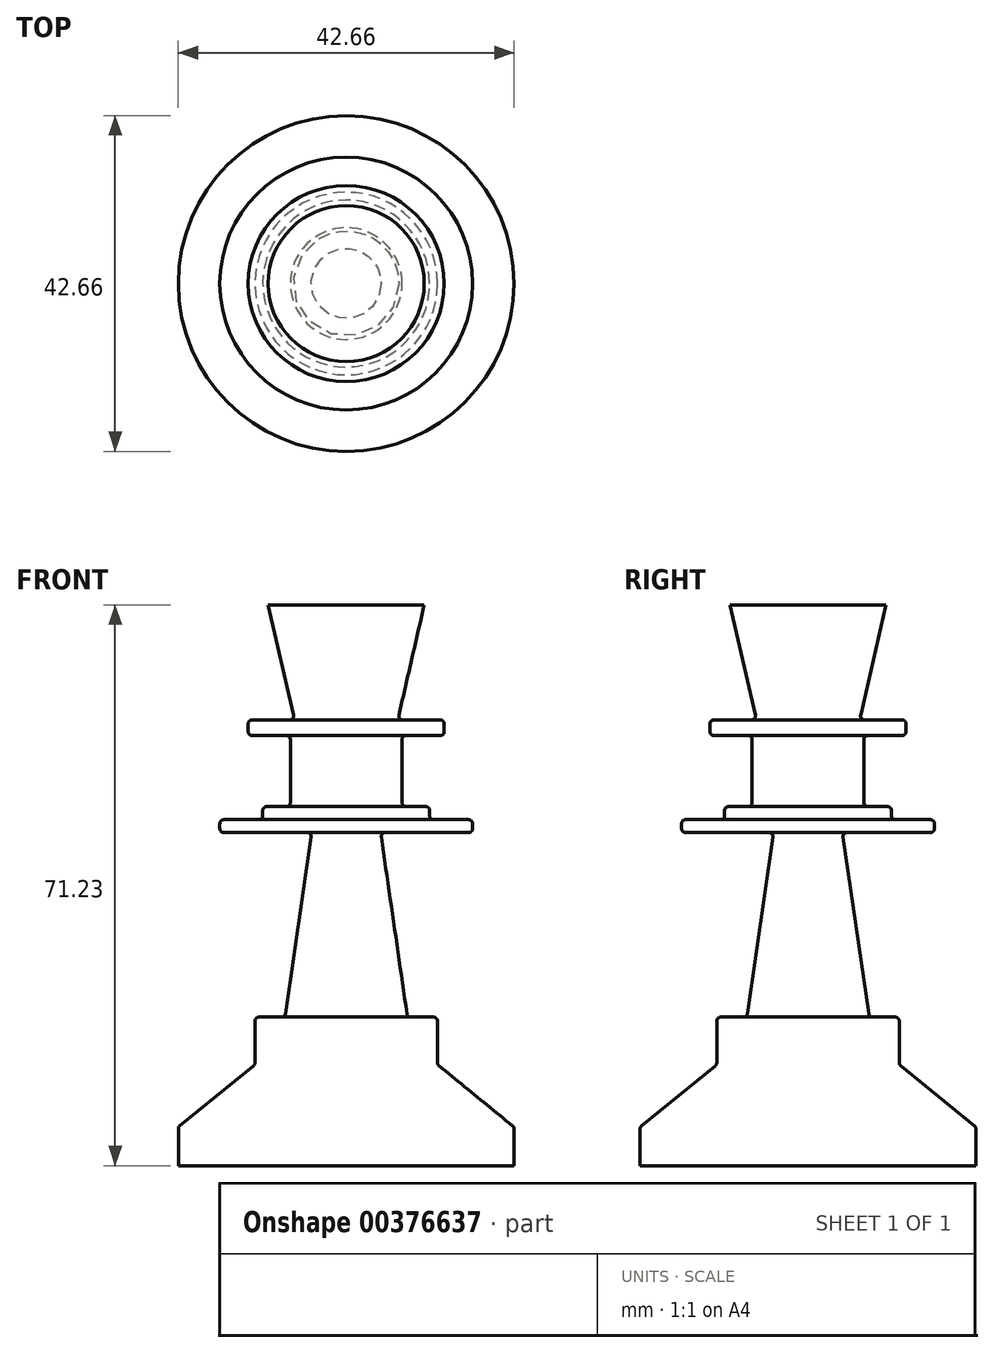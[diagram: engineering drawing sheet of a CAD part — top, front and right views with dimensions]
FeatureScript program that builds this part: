
annotation { "Feature Type Name" : "Feature", "Feature Type Description" : "" }
export const myFeature = defineFeature(function(context is Context, id is Id, definition is map)
    precondition{}
    {
        {
            var Q0;
            Q0=qCreatedBy(makeId("Front.planeOp"),FACE);
            var sketch = newSketch(context, id + "F0", { "sketchPlane" : qUnion([Q0])});
            skLineSegment(sketch, "E0", {"start": v(0, 71.23) * mm, "end": v(-9.91, 71.23) * mm});
            skLineSegment(sketch, "E1", {"start": v(-9.91, 71.23) * mm, "end": v(-6.7, 57.26) * mm});
            skLineSegment(sketch, "E2", {"start": v(-7.19, 56.63) * mm, "end": v(-11.95, 56.63) * mm});
            skLineSegment(sketch, "E3", {"start": v(-12.45, 56.13) * mm, "end": v(-12.45, 55.15) * mm});
            skLineSegment(sketch, "E4", {"start": v(-11.95, 54.64) * mm, "end": v(-7.6, 54.64) * mm});
            skLineSegment(sketch, "E5", {"start": v(-7.1, 54.13) * mm, "end": v(-7.1, 46.13) * mm});
            skLineSegment(sketch, "E6", {"start": v(-7.6, 45.63) * mm, "end": v(-10.1, 45.63) * mm});
            skLineSegment(sketch, "E7", {"start": v(-10.6, 45.12) * mm, "end": v(-10.6, 44.46) * mm});
            skLineSegment(sketch, "E8", {"start": v(-11.1, 43.95) * mm, "end": v(-15.55, 43.95) * mm});
            skLineSegment(sketch, "E9", {"start": v(-16.06, 43.45) * mm, "end": v(-16.06, 42.82) * mm});
            skLineSegment(sketch, "E10", {"start": v(-15.55, 42.31) * mm, "end": v(-4.96, 42.31) * mm});
            skLineSegment(sketch, "E11", {"start": v(-4.45, 41.73) * mm, "end": v(-7.71, 19.3) * mm});
            skLineSegment(sketch, "E12", {"start": v(-21.33, 4.66) * mm, "end": v(-21.33, 0) * mm});
            skLineSegment(sketch, "E13", {"start": v(-21.33, 0) * mm, "end": v(0, 0) * mm});
            skLineSegment(sketch, "E14", {"start": v(-8.22, 18.87) * mm, "end": v(-11.09, 18.87) * mm});
            skLineSegment(sketch, "E15", {"start": v(-11.6, 18.37) * mm, "end": v(-11.6, 13.08) * mm});
            skLineSegment(sketch, "E16", {"start": v(-21.14, 5.05) * mm, "end": v(-11.78, 12.69) * mm});
            skLineSegment(sketch, "E17", {"start": v(0, 71.23) * mm, "end": v(0, 0) * mm});
            skPoint(sketch, "E18.visualSharp", {"position": v(-6.55, 56.63) * mm});
            skArc(sketch, "E18.filletArc", {"start": v(-7.19, 56.63) * mm, "mid": v(-6.79, 56.82) * mm, "end": v(-6.7, 57.26) * mm});
            skPoint(sketch, "E19.visualSharp", {"position": v(-12.45, 56.63) * mm});
            skArc(sketch, "E19.filletArc", {"start": v(-11.95, 56.63) * mm, "mid": v(-12.3, 56.48) * mm, "end": v(-12.45, 56.13) * mm});
            skPoint(sketch, "E20.visualSharp", {"position": v(-12.45, 54.64) * mm});
            skArc(sketch, "E20.filletArc", {"start": v(-12.45, 55.15) * mm, "mid": v(-12.3, 54.79) * mm, "end": v(-11.95, 54.64) * mm});
            skPoint(sketch, "E21.visualSharp", {"position": v(-7.1, 54.64) * mm});
            skArc(sketch, "E21.filletArc", {"start": v(-7.1, 54.13) * mm, "mid": v(-7.25, 54.5) * mm, "end": v(-7.6, 54.64) * mm});
            skPoint(sketch, "E22.visualSharp", {"position": v(-7.1, 45.63) * mm});
            skArc(sketch, "E22.filletArc", {"start": v(-7.6, 45.63) * mm, "mid": v(-7.25, 45.78) * mm, "end": v(-7.1, 46.13) * mm});
            skPoint(sketch, "E23.visualSharp", {"position": v(-10.6, 45.63) * mm});
            skArc(sketch, "E23.filletArc", {"start": v(-10.1, 45.63) * mm, "mid": v(-10.45, 45.48) * mm, "end": v(-10.6, 45.12) * mm});
            skPoint(sketch, "E24.visualSharp", {"position": v(-10.6, 43.95) * mm});
            skArc(sketch, "E24.filletArc", {"start": v(-11.1, 43.95) * mm, "mid": v(-10.75, 44.1) * mm, "end": v(-10.6, 44.46) * mm});
            skPoint(sketch, "E25.visualSharp", {"position": v(-16.06, 43.95) * mm});
            skArc(sketch, "E25.filletArc", {"start": v(-15.55, 43.95) * mm, "mid": v(-15.9, 43.8) * mm, "end": v(-16.06, 43.45) * mm});
            skPoint(sketch, "E26.visualSharp", {"position": v(-16.06, 42.31) * mm});
            skArc(sketch, "E26.filletArc", {"start": v(-16.06, 42.82) * mm, "mid": v(-15.9, 42.46) * mm, "end": v(-15.55, 42.31) * mm});
            skPoint(sketch, "E27.visualSharp", {"position": v(-4.37, 42.31) * mm});
            skArc(sketch, "E27.filletArc", {"start": v(-4.45, 41.73) * mm, "mid": v(-4.57, 42.14) * mm, "end": v(-4.96, 42.31) * mm});
            skPoint(sketch, "E28.visualSharp", {"position": v(-7.78, 18.87) * mm});
            skArc(sketch, "E28.filletArc", {"start": v(-8.22, 18.87) * mm, "mid": v(-7.88, 19) * mm, "end": v(-7.71, 19.3) * mm});
            skPoint(sketch, "E29.visualSharp", {"position": v(-11.6, 18.87) * mm});
            skArc(sketch, "E29.filletArc", {"start": v(-11.09, 18.87) * mm, "mid": v(-11.44, 18.72) * mm, "end": v(-11.6, 18.37) * mm});
            skPoint(sketch, "E30.visualSharp", {"position": v(-11.6, 12.84) * mm});
            skArc(sketch, "E30.filletArc", {"start": v(-11.78, 12.69) * mm, "mid": v(-11.64, 12.86) * mm, "end": v(-11.6, 13.08) * mm});
            skPoint(sketch, "E31.visualSharp", {"position": v(-21.33, 4.9) * mm});
            skArc(sketch, "E31.filletArc", {"start": v(-21.14, 5.05) * mm, "mid": v(-21.28, 4.88) * mm, "end": v(-21.33, 4.66) * mm});
            skSolve(sketch);
        }
        {
            var Q0;
            Q0=makeQuery(id+"F0.imprint","IMPRINT",FACE,{"disambiguationData":[TD([[makeQuery(id+"F0.imprint","IMPRINT",EDGE,{"derivedFrom":sQuery(id+"F0.wireOp",EDGE,"E0")}),1.0]])]});
            var Q1;
            Q1=sQuery(id+"F0.wireOp",EDGE,"E17");
            revolve(context, id + "F1", {"entities" : qUnion([Q0]), "axis" : qUnion([Q1]), "revolveType" : RevolveType.FULL});
        }
    });
